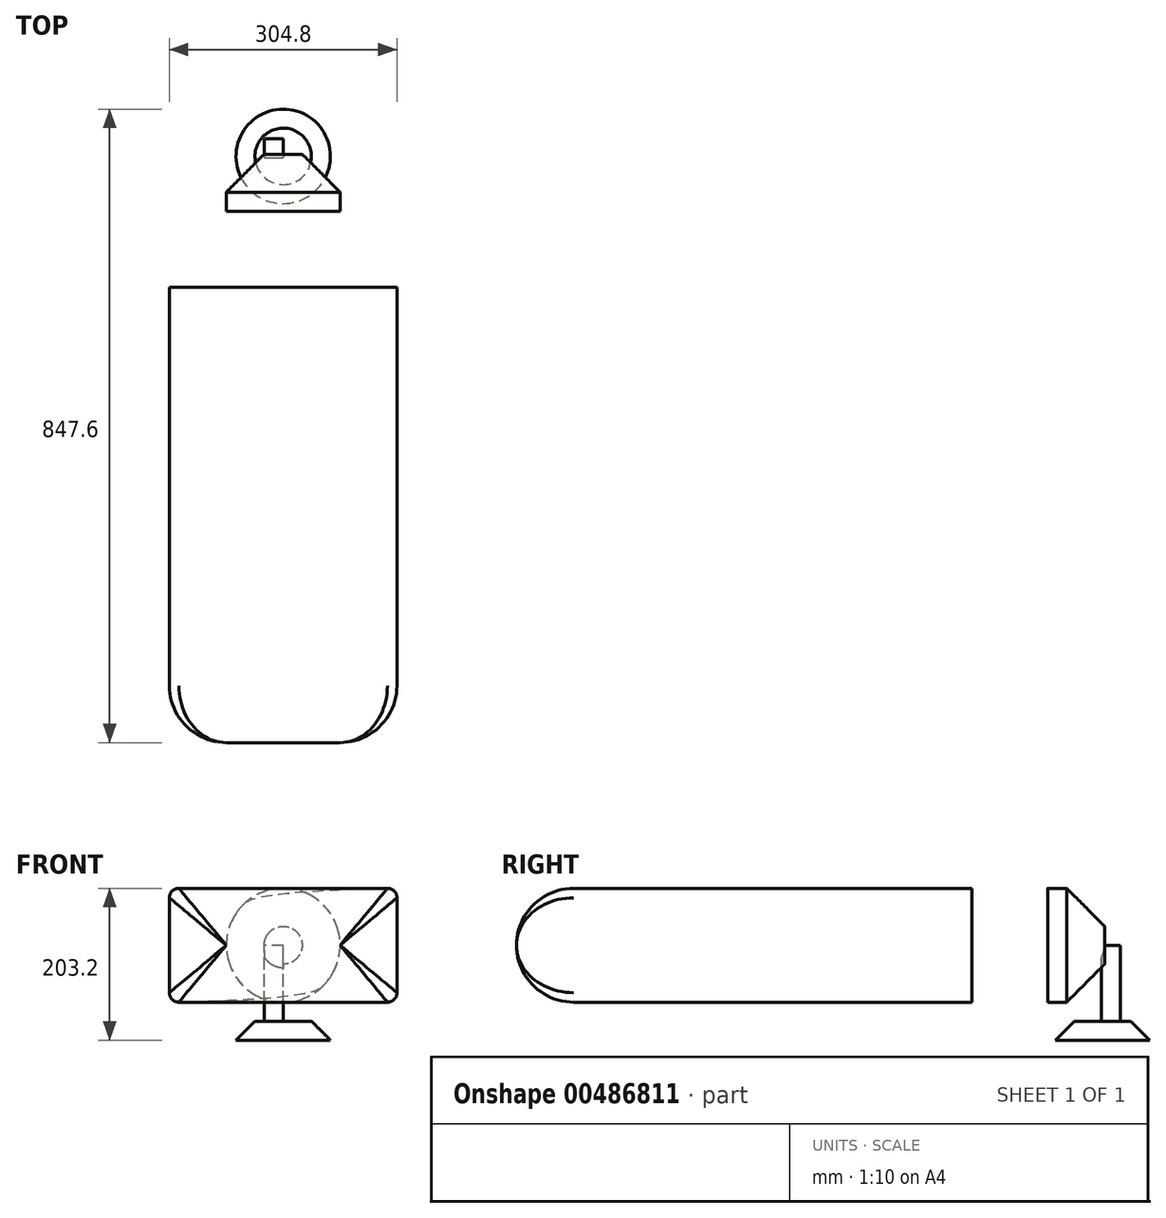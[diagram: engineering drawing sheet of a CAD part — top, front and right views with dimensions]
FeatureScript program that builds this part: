
annotation { "Feature Type Name" : "Feature", "Feature Type Description" : "" }
export const myFeature = defineFeature(function(context is Context, id is Id, definition is map)
    precondition{}
    {
        {
            var Q0;
            Q0=qCreatedBy(makeId("Front.planeOp"),FACE);
            var sketch = newSketch(context, id + "F0", { "sketchPlane" : qUnion([Q0])});
            skCircle(sketch, "E0", {"center": v(0, 0) * mm, "radius": 76.2 * mm});
            skSolve(sketch);
        }
        {
            var Q0;
            Q0=qCreatedBy(makeId("Front.planeOp"),FACE);
            cPlane(context, id + "F1", {"entities" : qUnion([Q0]), "cplaneType" : CPlaneType.OFFSET, "offset" : 101.6 * mm, "width" : 152.4 * mm, "height" : 152.4 * mm});
        }
        {
            var Q0;
            Q0=qCreatedBy(id+"F1.planeOp",FACE);
            var sketch = newSketch(context, id + "F2", { "sketchPlane" : qUnion([Q0])});
            skLineSegment(sketch, "E1.bottom", {"start": v(139.7, -76.2) * mm, "end": v(-139.7, -76.2) * mm});
            skLineSegment(sketch, "E1.top", {"start": v(139.7, 76.2) * mm, "end": v(-139.7, 76.2) * mm});
            skLineSegment(sketch, "E1.left", {"start": v(152.4, -63.5) * mm, "end": v(152.4, 63.5) * mm});
            skLineSegment(sketch, "E1.right", {"start": v(-152.4, -63.5) * mm, "end": v(-152.4, 63.5) * mm});
            skPoint(sketch, "E1.middle", {"position": v(0, 0) * mm});
            skPoint(sketch, "E2.visualSharp", {"position": v(-152.4, 76.2) * mm});
            skArc(sketch, "E2.filletArc", {"start": v(-139.7, 76.2) * mm, "mid": v(-148.68, 72.48) * mm, "end": v(-152.4, 63.5) * mm});
            skPoint(sketch, "E3.visualSharp", {"position": v(-152.4, -76.2) * mm});
            skArc(sketch, "E3.filletArc", {"start": v(-152.4, -63.5) * mm, "mid": v(-148.68, -72.48) * mm, "end": v(-139.7, -76.2) * mm});
            skPoint(sketch, "E4.visualSharp", {"position": v(152.4, -76.2) * mm});
            skArc(sketch, "E4.filletArc", {"start": v(139.7, -76.2) * mm, "mid": v(148.68, -72.48) * mm, "end": v(152.4, -63.5) * mm});
            skPoint(sketch, "E5.visualSharp", {"position": v(152.4, 76.2) * mm});
            skArc(sketch, "E5.filletArc", {"start": v(152.4, 63.5) * mm, "mid": v(148.68, 72.48) * mm, "end": v(139.7, 76.2) * mm});
            skSolve(sketch);
        }
        {
            var Q0;
            Q0=makeQuery(id+"F0.imprint","IMPRINT",FACE,{"disambiguationData":[TD([[makeQuery(id+"F0.imprint","IMPRINT",EDGE,{"derivedFrom":sQuery(id+"F0.wireOp",EDGE,"E0")}),1.0]])]});
            var Q1;
            Q1=makeQuery(id+"F2.imprint","IMPRINT",FACE,{"disambiguationData":[TD([[makeQuery(id+"F2.imprint","IMPRINT",EDGE,{"derivedFrom":sQuery(id+"F2.wireOp",EDGE,"E1.bottom")}),-1.0]])]});
            loft(context, id + "F3", {"sheetProfilesArray" : [{ "sheetProfileEntities" : qUnion([Q0]) }, { "sheetProfileEntities" : qUnion([Q1]) }]});
        }
        {
            var Q0;
            Q0=makeQuery(id+"F3.opLoft","CAP_FACE",FACE,{"disambiguationData":[OSD([makeQuery(id+"F2.imprint","IMPRINT",FACE,{"disambiguationData":[TD([[makeQuery(id+"F2.imprint","IMPRINT",EDGE,{"derivedFrom":sQuery(id+"F2.wireOp",EDGE,"E1.bottom")}),-1.0]])]})])],"isStart":true});
            extrude(context, id + "F4", {"entities" : qUnion([Q0]), "operationType" : NewBodyOperationType.ADD, "depth" : 609.6 * mm, "offsetDistance" : 25.4 * mm});
        }
        {
            var Q0;
            Q0=makeQuery(id+"F3.opLoft","CAP_FACE",FACE,{"disambiguationData":[OSD([makeQuery(id+"F0.imprint","IMPRINT",FACE,{"disambiguationData":[TD([[makeQuery(id+"F0.imprint","IMPRINT",EDGE,{"derivedFrom":sQuery(id+"F0.wireOp",EDGE,"E0")}),1.0]])]})])],"isStart":true});
            extrude(context, id + "F5", {"entities" : qUnion([Q0]), "operationType" : NewBodyOperationType.ADD, "depth" : 76.2 * mm, "offsetDistance" : 25.4 * mm});
        }
        {
            var Q0;
            Q0=makeQuery(id+"F5.opExtrude","CAP_FACE",FACE,{"disambiguationData":[OSD([makeQuery(id+"F0.imprint","IMPRINT",FACE,{"disambiguationData":[TD([[makeQuery(id+"F0.imprint","IMPRINT",EDGE,{"derivedFrom":sQuery(id+"F0.wireOp",EDGE,"E0")}),1.0]])]})])],"isStart":false});
            chamfer(context, id + "F6", {"entities" : qUnion([Q0]), "width" : 50.8 * mm, "tangentPropagation" : true});
        }
        {
            var Q0;
            Q0=makeQuery(id+"F4.opExtrude","CAP_FACE",FACE,{"disambiguationData":[OSD([makeQuery(id+"F2.imprint","IMPRINT",FACE,{"disambiguationData":[TD([[makeQuery(id+"F2.imprint","IMPRINT",EDGE,{"derivedFrom":sQuery(id+"F2.wireOp",EDGE,"E1.bottom")}),-1.0]])]})])],"isStart":false});
            fillet(context, id + "F7", {"entities" : qUnion([Q0]), "radius" : 76.2 * mm, "tangentPropagation" : true, "allowEdgeOverflow" : false});
        }
        {
            var Q0;
            Q0=qCreatedBy(makeId("Top.planeOp"),FACE);
            var sketch = newSketch(context, id + "F8", { "sketchPlane" : qUnion([Q0])});
            skLineSegment(sketch, "E6.bottom", {"start": v(0, 71.67) * mm, "end": v(-25.4, 71.67) * mm});
            skLineSegment(sketch, "E6.top", {"start": v(0, 97.07) * mm, "end": v(-25.4, 97.07) * mm});
            skLineSegment(sketch, "E6.left", {"start": v(0, 71.67) * mm, "end": v(0, 97.07) * mm});
            skLineSegment(sketch, "E6.right", {"start": v(-25.4, 71.67) * mm, "end": v(-25.4, 97.07) * mm});
            skSolve(sketch);
        }
        {
            var Q0;
            Q0=makeQuery(id+"F8.imprint","IMPRINT",FACE,{"disambiguationData":[TD([[makeQuery(id+"F8.imprint","IMPRINT",EDGE,{"derivedFrom":sQuery(id+"F8.wireOp",EDGE,"E6.bottom")}),-1.0]])]});
            var Q1;
            Q1=makeQuery(id+"F4.opExtrude","SWEPT_FACE",FACE,{"disambiguationData":[OSD([sQuery(id+"F2.wireOp",EDGE,"E1.top"),sQuery(id+"F2.wireOp",EDGE,"E2.filletArc"),sQuery(id+"F2.wireOp",EDGE,"E5.filletArc")])]});
            extrude(context, id + "F9", {"entities" : qUnion([Q0, Q1]), "operationType" : NewBodyOperationType.ADD, "oppositeDirection" : true, "depth" : 127 * mm, "offsetDistance" : 25.4 * mm});
        }
        {
            var Q0;
            Q0=qCreatedBy(makeId("Top.planeOp"),FACE);
            cPlane(context, id + "F10", {"entities" : qUnion([Q0]), "cplaneType" : CPlaneType.OFFSET, "offset" : 127 * mm, "oppositeDirection" : true, "width" : 152.4 * mm, "height" : 152.4 * mm});
        }
        {
            var Q0;
            Q0=qCreatedBy(id+"F10.planeOp",FACE);
            var sketch = newSketch(context, id + "F11", { "sketchPlane" : qUnion([Q0])});
            skCircle(sketch, "E7", {"center": v(0, 73.22) * mm, "radius": 63.18 * mm});
            skSolve(sketch);
        }
        {
            var Q0;
            Q0=makeQuery(id+"F11.imprint","IMPRINT",FACE,{"disambiguationData":[TD([[makeQuery(id+"F11.imprint","IMPRINT",EDGE,{"derivedFrom":sQuery(id+"F11.wireOp",EDGE,"E7")}),1.0]])]});
            extrude(context, id + "F12", {"entities" : qUnion([Q0]), "operationType" : NewBodyOperationType.ADD, "depth" : 25.4 * mm, "offsetDistance" : 25.4 * mm});
        }
        {
            var Q0;
            Q0=makeQuery(id+"F12.opExtrude","CAP_EDGE",EDGE,{"disambiguationData":[OSD([sQuery(id+"F11.wireOp",EDGE,"E7")])],"isStart":false});
            chamfer(context, id + "F13", {"entities" : qUnion([Q0]), "width" : 25.4 * mm, "tangentPropagation" : true});
        }
    });
